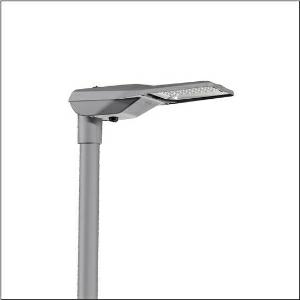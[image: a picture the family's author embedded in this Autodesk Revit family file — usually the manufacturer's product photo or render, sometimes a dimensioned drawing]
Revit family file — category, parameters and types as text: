
# Revit family: streetlight_sl_21_mini___st0_5a_5xe2b43t08gb_315d
name_source: partatom
category: Lighting Fixtures
units: mm (PartAtom-declared; Revit-internal decimal feet)

## family parameters
Cut with Voids When Loaded = No
Host = Face
Light Source = No
Part Type = Normal
Room Calculation Point = No
Round Connector Dimension = Use Diameter
Shared = No

## types (1)
- --- (1 x LED, 6180 lm, 40.4 W, 4000K)
    Apparent Load = 40 VA
    CIE Flux Codes = 41 75 97 100 100
    Color Rendering = 70
    Color Temperature = 4000K
    Default Elevation = 1800 mm
    Description = Streetlight SL 21 mini, mast luminaire, primary light control with lens, of PMMA, primary optical cover: cover, of toughened safety glass, transparent, light distribution: ST0.5a, light emission: direct distribution, primary light characteristic: asymmetric, installation type: side-entry, post-top, LED, High Power LED, rated luminous flux: 6.180lm, luminous efficacy: 153lm/W, light colour: 740, colour temperature: 4000K, control gear: D4i, control: overheat protection, constant luminous flux control, time-dependent luminous flux control, flexible luminous flux parameterisation, pre-setting: logarithmic dimming characteristic, mains connection: 220..240V, AC, 50/60Hz, start of lifetime: 40W, end of service life: 41W, reduction: 19W, luminaire housing, of diecast aluminium, powder-coated, SITECO metallic grey (DB 702S), corrosivity category C5 high according to DIN EN ISO 12944, please order mast flange separately, inclination adjustable: 0°, 5°, 10°, 15°, sealing non-destructively replaceable, multi-level sealing system, length: 628mm, width: 235mm, height: 110mm, mast flange for spigot size: 42mm (side-entry): 5XC10008XM4, 60/48mm (side-entry/post-top): 5XC10108XM2, 76/60mm (side-entry/post-top): 5XC10108XM1, mounting height: 4..8m, Smart Interface below and above, protection rating (complete): IP66, insulation class (complete): insulation class II (safety insulation), certification: CE, ENEC, ENEC+, VDE, impact resistance: IK10, permissible operating ambient temperature for outdoor applications: -40..+50°C, standard-compliant lighting for roads and squares, packaging unit: 1 piece

Light Distribution: ST0.5a
    Height = 110 mm
    Lamp = 1 x LED
    Lamp Light Flux = 6180 lm
    Lamp Power = 40.4 W
    Lamp count = 1
    Length = 625 mm
    Luminous efficacy = 153 lm/W
    Manufacturer = Siteco
    ModVariant = No
    Model = 5XE2B43T08GB
    Number of Poles = 1
    OnlyDefault = Yes
    Power Factor = 1
    Product Name = Streetlight SL 21 mini | ST0.5a
    Product group = mast luminaire | pylon top
    ProductGroupID = 6100
    Protection Class = Protection class II
    Protection Degree = IP 66
    RLX_Detail_Level = 1
    RLX_Emergency_Light_Flux = 0 lm
    RLX_Emergency_Type = 0
    RLX_Emergency_Type_DB = No
    RlxData = <blob elided: 37289 chars, md5=bacd9d57>
    Socket = socket
    Standby Power = 0 W
    System Light Flux = 6180 lm
    System Power = 40 W
    Type Comments = factory setting: luminous flux: 100 % | dim-lin: 254 | 812 mA
    Type Image = l_1003514.jpg
    URL = http://relux.com
    VarID = @adj_188539
    Voltage = 0 V
    Weight = 0.00 kg
    Width = 234 mm

## geometry (parser evidence)
native form markers: Blend x4, Sweep x10
no freeform markers — native parametric forms only
